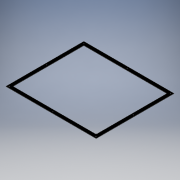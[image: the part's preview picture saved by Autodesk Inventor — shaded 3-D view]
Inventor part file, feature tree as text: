
AUTODESK INVENTOR PART (.ipt)
format: ipt  version: 2017.3 (Build 213256000, 256)  size: 150,528 bytes
history: native  units: mm
features: sheet_metal_op x1, sketch x1, other x1
ambient origin geometry x8: Origin, YZ Plane, XZ Plane, XY Plane, X Axis, Y Axis, Z Axis, Center Point
bodies: Body1 (feature_tree)
feature tree (3):
  sheet_metal_op  "Face6"
  sketch  "Sketch1"  dims[d0=513.0mm d1=443.0mm d2=10.0mm d3=10.0mm d4=10.0mm d5=110.0mm d6=80.0mm d7=110.0mm d8=110.0mm d9=70.0mm d10=55.0mm d12=1.5mm d13=1.5mm d16=1.5mm d19=1.5mm d20=1.5mm d23=10.0mm d24=10.0mm d25=20.0mm d26=10.0mm d27=2.0mm d28=5.0mm d29=4.2mm d30=10.0mm d31=1.5mm]
  other  "Plate6"
